# Revit family: Accessory-Towel_Ring-KALLISTA-PINNA_PALETTA-P25336_1
name_source: partatom
category: Specialty Equipment
units: mm (PartAtom-declared; Revit-internal decimal feet)

## family parameters
Cut with Voids When Loaded = No
Host = Face
Maintain Annotation Orientation = No
OmniClass Number = 23.31.25.00
Part Type = Normal
Room Calculation Point = No
Round Connector Dimension = Use Diameter
Shared = No

## types (6) — shared parameters
ADA Compliant = No
Assembly Code = C1030200
Date Modified = 11/24/2023
Default Elevation = 42"
Description = Towel Ring
Height = 5 9/16"
Length = 2 5/16"
Manufacturer = Kallista Co.
Master Format 2014 = 10 28 00
Master Format 2014 Name = Toilet, Bath, and Laundry Accessories
Material = Premium Metal Construction
Product Documentation Link = https://resources.kohler.com
Product Name = PINNA PALETTA
URL = http://www.kallista.com
WaterSense Certified = No
Width = 7 3/16"

## per-type parameters (varying)
| type | Finish | Model | Product Page URL | Secondary Finish | Type |
| BAF, BAF-Brushed French Gold | Kallista-Metal-BAF-Brushed_French_Gold | P25336-BAF-BAF | https://www.kallista.com | Kallista-Metal-BAF-Brushed_French_Gold | 1 |
| CPH, CP-Chrome | Kallista-Metal-CP-Chrome | P25336-CPH-CP | https://www.kallista.com | Kallista-Metal-CPH-Polished_Chrome | 2 |
| SNW, SN-Polished Nickel | Kallista-Metal-SN-Polished_Nickel | P25336-SNW-SN | https://www.kallista.com | Kallista-Metal-SNW-Polished_Nickel | 3 |
| ULB, ULB-Unlaquered Brass | Kallista-Metal-ULB-Unlaquered_Brass | P25336-ULB-ULB | https://www.kallista.com | Kallista-Metal-ULB-Unlaquered_Brass | 4 |
| BAF, BN-Brushed Nickel | Kallista-Metal-BAF-Brushed_French_Gold | P25336-BAF-BN |  | Kallista-Metal-BN-Brushed_Nickel | 5 |
| BNW, BN-Brushed Nickel | Kallista-Metal-BNW-Brushed_Nickel | P25336-BNW-BN |  | Kallista-Metal-BN-Brushed_Nickel | 6 |

## geometry (parser evidence)
native form markers: Sweep x4
no freeform markers — native parametric forms only
